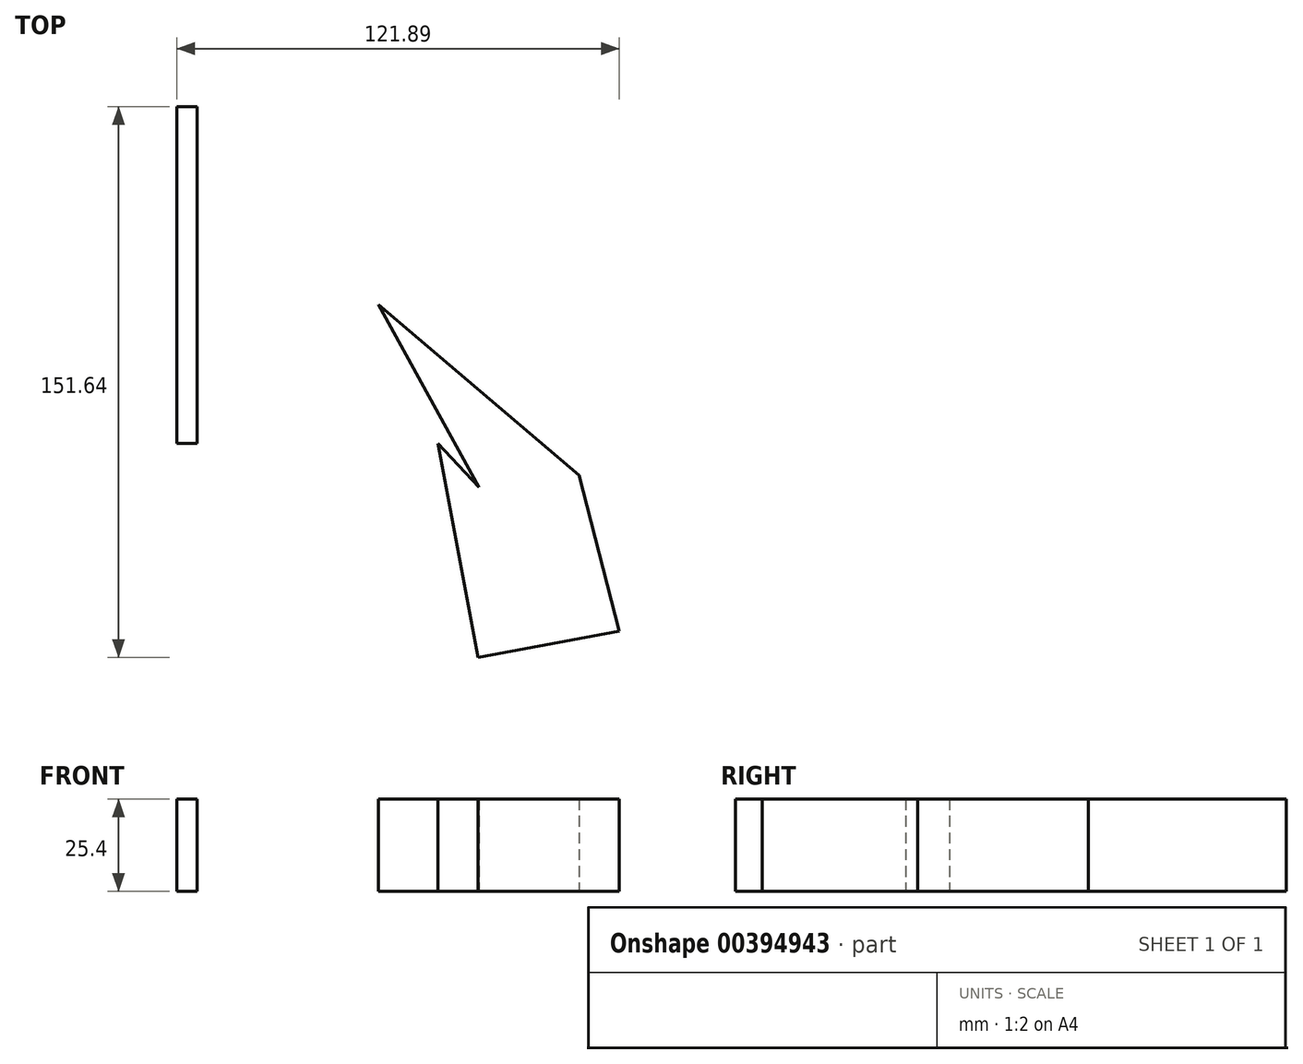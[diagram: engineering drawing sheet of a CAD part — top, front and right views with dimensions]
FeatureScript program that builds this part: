
annotation { "Feature Type Name" : "Feature", "Feature Type Description" : "" }
export const myFeature = defineFeature(function(context is Context, id is Id, definition is map)
    precondition{}
    {
        {
            var Q0;
            Q0=qCreatedBy(makeId("Top.planeOp"),FACE);
            var sketch = newSketch(context, id + "F0", { "sketchPlane" : qUnion([Q0])});
            skLineSegment(sketch, "E0", {"start": v(0, 0) * mm, "end": v(11.04, -58.92) * mm});
            skLineSegment(sketch, "E1", {"start": v(11.04, -58.92) * mm, "end": v(49.97, -51.63) * mm});
            skLineSegment(sketch, "E2", {"start": v(49.97, -51.63) * mm, "end": v(38.85, -8.8) * mm});
            skLineSegment(sketch, "E3", {"start": v(38.85, -8.8) * mm, "end": v(-16.4, 38.24) * mm});
            skLineSegment(sketch, "E4", {"start": v(-16.4, 38.24) * mm, "end": v(11.28, -12.1) * mm});
            skLineSegment(sketch, "E5", {"start": v(11.28, -12.1) * mm, "end": v(0, 0) * mm});
            skLineSegment(sketch, "E6.bottom", {"start": v(-66.27, 0) * mm, "end": v(-71.92, 0) * mm});
            skLineSegment(sketch, "E6.top", {"start": v(-66.27, 92.72) * mm, "end": v(-71.92, 92.72) * mm});
            skLineSegment(sketch, "E6.left", {"start": v(-66.27, 0) * mm, "end": v(-66.27, 92.72) * mm});
            skLineSegment(sketch, "E6.right", {"start": v(-71.92, 0) * mm, "end": v(-71.92, 92.72) * mm});
            skSolve(sketch);
        }
        {
            var Q0;
            Q0 = qSketchRegion(id + "F0", true);
            extrude(context, id + "F1", {"entities" : qUnion([Q0]), "depth" : 25.4 * mm});
        }
    });
